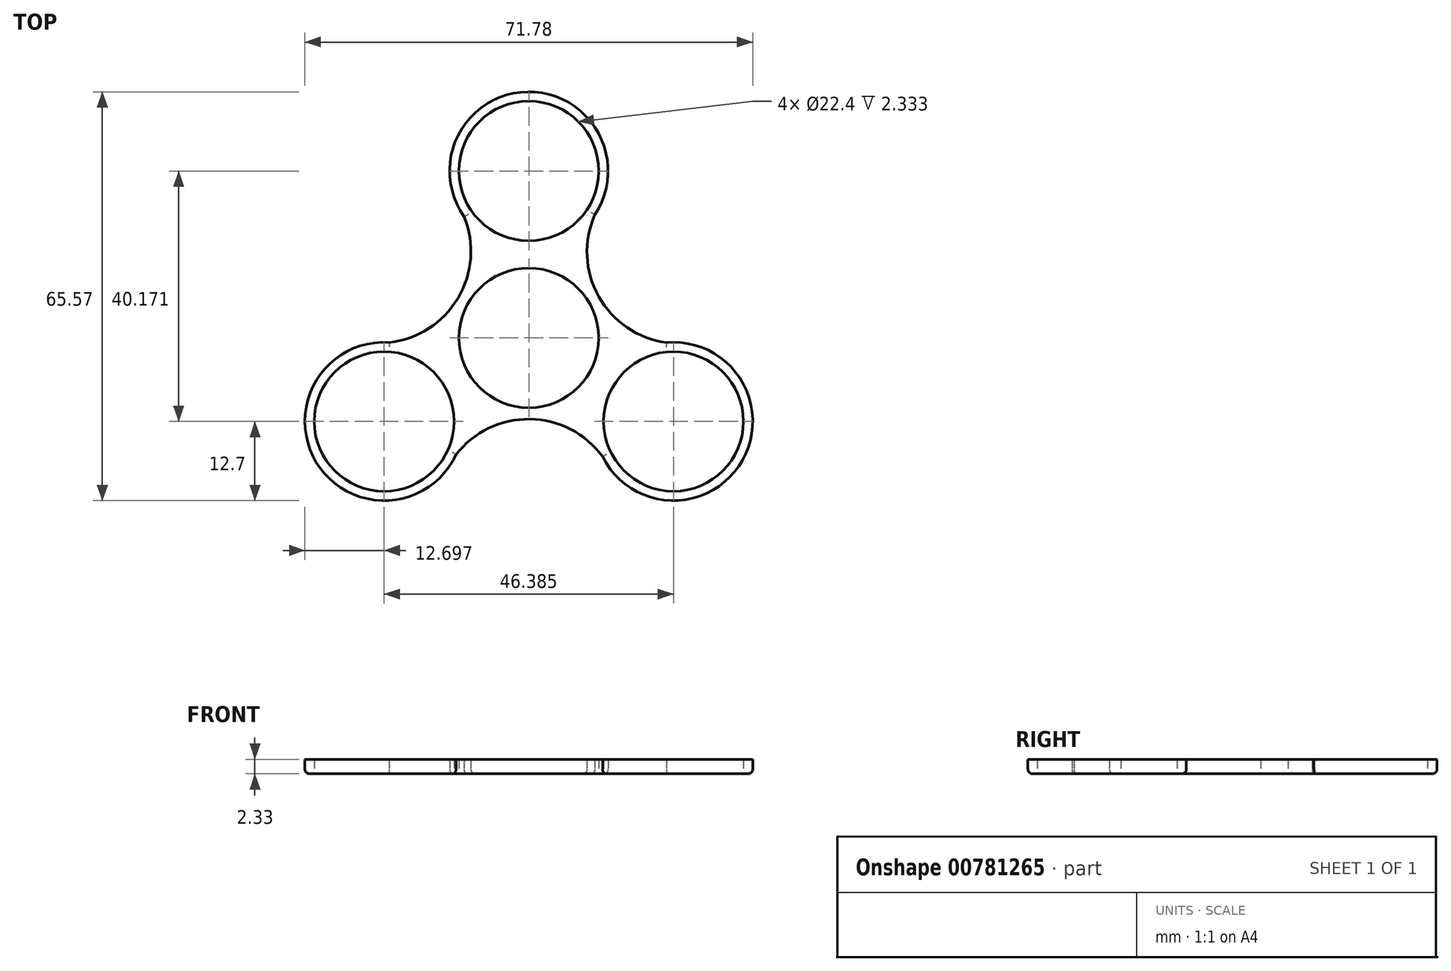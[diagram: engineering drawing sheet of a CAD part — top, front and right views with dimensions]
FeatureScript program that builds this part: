
annotation { "Feature Type Name" : "Feature", "Feature Type Description" : "" }
export const myFeature = defineFeature(function(context is Context, id is Id, definition is map)
    precondition{}
    {
        {
            var Q0;
            Q0=qCreatedBy(makeId("Top.planeOp"),FACE);
            var sketch = newSketch(context, id + "F0", { "sketchPlane" : qUnion([Q0])});
            skCircle(sketch, "E0", {"center": v(0, 0) * mm, "radius": 11.2 * mm});
            skCircle(sketch, "E1", {"center": v(0, 26.78) * mm, "radius": 11.2 * mm});
            skArc(sketch, "E2", {"start": v(10.58, 19.75) * mm, "mid": v(-0.18, 39.48) * mm, "end": v(-10.38, 19.46) * mm});
            skCircle(sketch, "E3.1.0", {"center": v(-23.2, -13.4) * mm, "radius": 11.2 * mm});
            skArc(sketch, "E3.1.1", {"start": v(-22.4, -0.72) * mm, "mid": v(-34.1, -19.9) * mm, "end": v(-11.66, -18.72) * mm});
            skCircle(sketch, "E3.2.0", {"center": v(23.2, -13.4) * mm, "radius": 11.2 * mm});
            skArc(sketch, "E3.2.1", {"start": v(11.82, -19.04) * mm, "mid": v(34.28, -19.59) * mm, "end": v(22.04, -0.74) * mm});
            skArc(sketch, "E4", {"start": v(10.58, 19.75) * mm, "mid": v(11.2, 6.65) * mm, "end": v(22.04, -0.74) * mm});
            skArc(sketch, "E5.1.0", {"start": v(-22.4, -0.72) * mm, "mid": v(-11.36, 6.38) * mm, "end": v(-10.38, 19.46) * mm});
            skArc(sketch, "E5.2.0", {"start": v(11.82, -19.04) * mm, "mid": v(0.16, -13.02) * mm, "end": v(-11.66, -18.72) * mm});
            skLineSegment(sketch, "E6.trimOffspring", {"start": v(11.04, 6.29) * mm, "end": v(11.63, 6.63) * mm});
            skSolve(sketch);
        }
        {
            var Q0;
            Q0=makeQuery(id+"F0.imprint","IMPRINT",FACE,{"disambiguationData":[TD([[makeQuery(id+"F0.imprint","IMPRINT",EDGE,{"derivedFrom":sQuery(id+"F0.wireOp",EDGE,"E0")}),-1.0]])]});
            extrude(context, id + "F1", {"entities" : qUnion([Q0]), "depth" : 2.33 * mm, "offsetDistance" : 25 * mm});
        }
        {
            var Q0;
            Q0=makeQuery(id+"F1.opExtrude","CAP_EDGE",EDGE,{"disambiguationData":[OSD([sQuery(id+"F0.wireOp",EDGE,"E3.1.1")])],"isStart":true});
            var Q1;
            Q1=makeQuery(id+"F1.opExtrude","CAP_EDGE",EDGE,{"disambiguationData":[OSD([sQuery(id+"F0.wireOp",EDGE,"E5.2.0")])],"isStart":true});
            var Q2;
            Q2=makeQuery(id+"F1.opExtrude","CAP_EDGE",EDGE,{"disambiguationData":[OSD([sQuery(id+"F0.wireOp",EDGE,"E3.2.1")])],"isStart":true});
            var Q3;
            Q3=makeQuery(id+"F1.opExtrude","CAP_EDGE",EDGE,{"disambiguationData":[OSD([sQuery(id+"F0.wireOp",EDGE,"E4")])],"isStart":true});
            var Q4;
            Q4=makeQuery(id+"F1.opExtrude","CAP_EDGE",EDGE,{"disambiguationData":[OSD([sQuery(id+"F0.wireOp",EDGE,"E2")])],"isStart":true});
            var Q5;
            Q5=makeQuery(id+"F1.opExtrude","CAP_EDGE",EDGE,{"disambiguationData":[OSD([sQuery(id+"F0.wireOp",EDGE,"E5.1.0")])],"isStart":true});
            fillet(context, id + "F2", {"entities" : qUnion([Q0, Q1, Q2, Q3, Q4, Q5]), "radius" : .75 * mm, "tangentPropagation" : true, "allowEdgeOverflow" : false});
        }
    });
